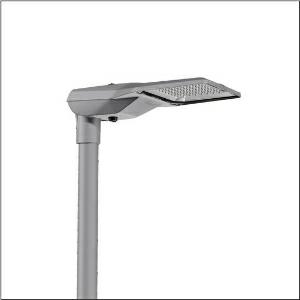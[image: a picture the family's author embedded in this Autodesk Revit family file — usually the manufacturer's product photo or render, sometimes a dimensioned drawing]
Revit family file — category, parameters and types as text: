
# Revit family: streetlight_sl_21_midi___p0_8ab_5xe3r33t08mb_ae32
name_source: partatom
category: Lighting Fixtures
units: mm (PartAtom-declared; Revit-internal decimal feet)

## family parameters
Cut with Voids When Loaded = No
Host = Face
Light Source = No
Part Type = Normal
Room Calculation Point = No
Round Connector Dimension = Use Diameter
Shared = No

## types (1)
- --- (1 x LED, 15870 lm, 136 W, 3000K)
    Apparent Load = 136 VA
    CIE Flux Codes = 36 71 98 100 100
    Color Rendering = 70
    Color Temperature = 3000K
    Default Elevation = 1800 mm
    Description = Streetlight SL 21 midi, mast luminaire, primary light control with lens, of PMMA, primary optical cover: cover, of toughened safety glass, transparent, light distribution: P0.8aB, light emission: direct distribution, primary light characteristic: asymmetric, installation type: post-top, side-entry, LED, High Power LED, rated luminous flux: 15.870lm, luminous efficacy: 117lm/W, light colour: 730, colour temperature: 3000K, control gear: D4i, control: pre-setting: logarithmic dimming characteristic, flexible luminous flux parameterisation, time-dependent luminous flux control, constant luminous flux control, overheat protection, mains connection: 230..240V, AC, 50/60Hz, start of lifetime: 136W, end of service life: 142W, reduction: 61W, luminaire housing, of diecast aluminium, powder-coated, Siteco® metallic grey (DB 702S), corrosivity category C5 mid according to DIN EN ISO 12944, multi-level sealing system, sealing non-destructively replaceable, inclination adjustable: 0°, 5°, 10°, 15°, please order mast flange separately, length: 644mm, width: 335mm, height: 110mm, mast flange for spigot size: 42mm (side-entry): 5XC10008XM4, 60/48mm (side-entry/post-top): 5XC10108XM2, 76/60mm (side-entry/post-top): 5XC10108XM1, mounting height: 4..8m, Smart Interface below and above, protection rating (complete): IP66, insulation class (complete): insulation class II (safety insulation), certification: CE, ENEC, ENEC+, VDE, impact resistance: IK09, permissible operating ambient temperature for outdoor applications: -40..+50°C, standard-compliant lighting for roads and squares, packaging unit: 1 piece

Light Distribution: P0.8aB
    Height = 111 mm
    Lamp = 1 x LED
    Lamp Light Flux = 15870 lm
    Lamp Power = 136 W
    Lamp count = 1
    Length = 644 mm
    Luminous efficacy = 117 lm/W
    Manufacturer = Siteco
    ModVariant = No
    Model = 5XE3R33T08MB
    Number of Poles = 1
    OnlyDefault = Yes
    Power Factor = 1
    Product Name = Streetlight SL 21 midi | P0.8aB
    Product group = mast luminaire | pylon top
    ProductGroupID = 6100
    Protection Class = Protection class II
    Protection Degree = IP 66
    RLX_Detail_Level = 1
    RLX_Emergency_Light_Flux = 0 lm
    RLX_Emergency_Type = 0
    RLX_Emergency_Type_DB = No
    RlxData = <blob elided: 90261 chars, md5=559aa663>
    Socket = socket
    Standby Power = 0 W
    System Light Flux = 15870 lm
    System Power = 136 W
    Type Comments = factory setting: luminous flux: 100 % | dim-lin: 254 | 695 mA
    Type Image = l_1004304.jpg
    URL = http://relux.com
    VarID = @adj_072080
    Voltage = 0 V
    Weight = 0.00 kg
    Width = 336 mm

## geometry (parser evidence)
native form markers: Blend x4, Sweep x11
no freeform markers — native parametric forms only
